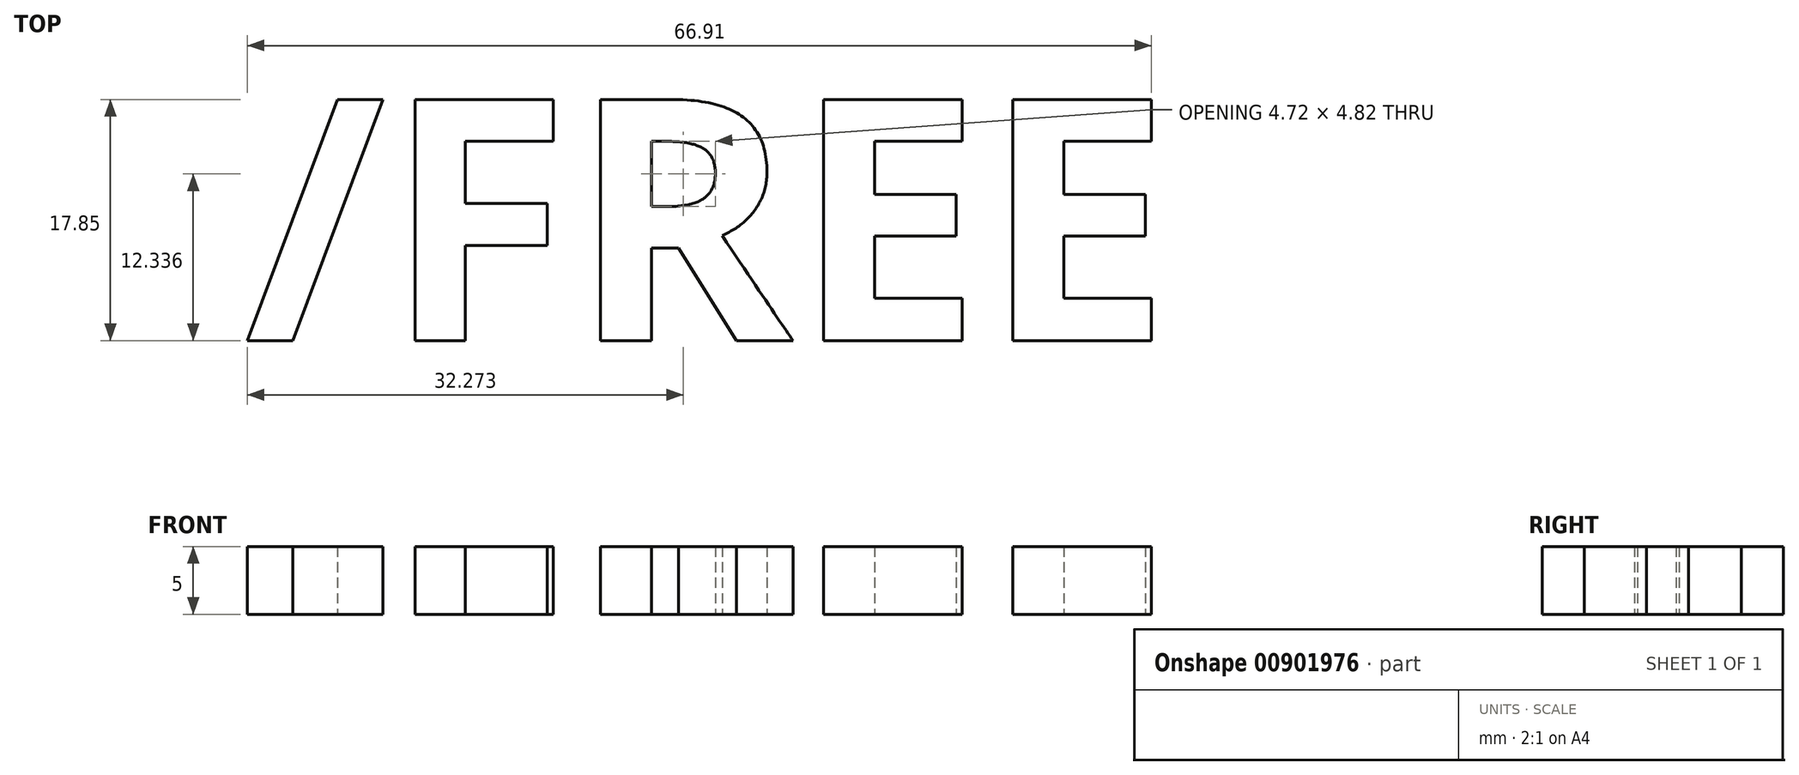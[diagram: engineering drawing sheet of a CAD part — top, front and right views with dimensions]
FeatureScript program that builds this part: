
annotation { "Feature Type Name" : "Feature", "Feature Type Description" : "" }
export const myFeature = defineFeature(function(context is Context, id is Id, definition is map)
    precondition{}
    {
        {
            var Q0;
            Q0=qCreatedBy(makeId("Top.planeOp"),FACE);
            var sketch = newSketch(context, id + "F0", { "sketchPlane" : qUnion([Q0])});
            skText(sketch, "E0", { "text": "/FREE", "fontName": "OpenSans-Bold.ttf"});
            const initialGuessF0  = {"E0": [-0.0148, -0.009, 1, 0, 0.018]};
            skSetInitialGuess(sketch, initialGuessF0);
            skSolve(sketch);
        }
        {
            var Q0;
            Q0=makeQuery(id+"F0.imprint","IMPRINT",FACE,{"disambiguationData":[TD([[makeQuery(id+"F0.imprint","IMPRINT",EDGE,{"derivedFrom":sQuery(id+"F0.wireOp",EDGE,"E0.sketch_text.stroke-0")}),-1.0]])]});
            var Q1;
            Q1=makeQuery(id+"F0.imprint","IMPRINT",FACE,{"disambiguationData":[TD([[makeQuery(id+"F0.imprint","IMPRINT",EDGE,{"derivedFrom":sQuery(id+"F0.wireOp",EDGE,"E0.sketch_text.stroke-4")}),-1.0]])]});
            var Q2;
            Q2=makeQuery(id+"F0.imprint","IMPRINT",FACE,{"disambiguationData":[TD([[makeQuery(id+"F0.imprint","IMPRINT",EDGE,{"derivedFrom":sQuery(id+"F0.wireOp",EDGE,"E0.sketch_text.stroke-14")}),-1.0]])]});
            var Q3;
            Q3=makeQuery(id+"F0.imprint","IMPRINT",FACE,{"disambiguationData":[TD([[makeQuery(id+"F0.imprint","IMPRINT",EDGE,{"derivedFrom":sQuery(id+"F0.wireOp",EDGE,"E0.sketch_text.stroke-33")}),-1.0]])]});
            var Q4;
            Q4=makeQuery(id+"F0.imprint","IMPRINT",FACE,{"disambiguationData":[TD([[makeQuery(id+"F0.imprint","IMPRINT",EDGE,{"derivedFrom":sQuery(id+"F0.wireOp",EDGE,"E0.sketch_text.stroke-45")}),-1.0]])]});
            extrude(context, id + "F1", {"entities" : qUnion([Q0, Q1, Q2, Q3, Q4]), "depth" : 5 * mm, "offsetDistance" : 25 * mm});
        }
    });
